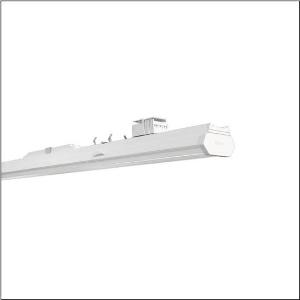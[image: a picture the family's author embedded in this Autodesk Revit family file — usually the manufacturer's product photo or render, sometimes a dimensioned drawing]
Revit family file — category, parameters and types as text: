
# Revit family: licross_11_protected_ho_51tp12dn5exm
name_source: partatom
category: Lighting Fixtures
units: mm (PartAtom-declared; Revit-internal decimal feet)

## family parameters
Cut with Voids When Loaded = No
Host = Face
Light Source = No
Part Type = Normal
Room Calculation Point = No
Round Connector Dimension = Use Diameter
Shared = No

## types (1)
- --- (1 x LED, 14100 lm, 81.2 W, 5000K)
    Apparent Load = 81 VA
    CIE Flux Codes = 70 91 97 98 100
    Color Rendering = 80
    Color Temperature = 5000K
    Default Elevation = 1800 mm
    Description = Licross 11 Protected HO, luminaire insert, of sheet steel, galvanised, coil coated, white, length: 1.500mm, width: 90mm, height: 101mm, LED rated luminous flux: 14.100lm, light colour: 850, SDCM (Standard Deviation of Colour Matching)MacAdam ≤ 2 SDCM (initial), control gear: DALI 2, with plug, 5-pole, with phase selection, mains connection: 220..240V, AC, 50/60Hz, rated input power: 81W, internal wiring halogen-free, primary optical cover: cover, of PMMA, light emission: direct distribution, primary light characteristic: symmetric, protection rating (complete): IP64, insulation class (complete): insulation class I (protective earthing), certification: CE, ENEC, VDE, UKCA, protection symbol: D if used in an environment with conductive dust loads with corresponding accessories, impact resistance: IK06, permissible ambient temperature for indoor applications: -25..+35°C, corresponds to IFS (International Featured Standards) requirements for safety and quality in the food industry, reducing of maximum allowable ambient temperature of 5°C with ceiling mounting, LABS conformity tested according to VDMA 24364:2018-05, The light source and the operating device comply with the requirements of the Ecodesign Regulation (EU) 2019/2020 and are replaceable in accordance with this regulation, packaging unit: 1 piece
    Height = 92 mm
    Lamp = 1 x LED
    Lamp Light Flux = 14100 lm
    Lamp Power = 81.2 W
    Lamp count = 1
    Length = 1500 mm
    Luminous efficacy = 174 lm/W
    Manufacturer = Siteco
    ModVariant = No
    Model = 51TP12DN5EXM
    Mounting Place = Ceiling
    Mounting Type = Pendant
    Number of Poles = 1
    OnlyDefault = Yes
    Power Factor = 1
    Product Name = Licross 11 Protected HO
    Product group = luminaire insert | ceiling pendant
    ProductGroupID = 901
    Protection Class = Protection class I
    Protection Degree = IP 64
    RLX_Detail_Level = 1
    RLX_Emergency_Light_Flux = 0 lm
    RLX_Emergency_Type = 0
    RLX_Emergency_Type_DB = No
    RlxData = <blob elided: 24781 chars, md5=22ba8a19>
    Socket = socket
    Standby Power = 0 W
    System Light Flux = 14100 lm
    System Power = 81 W
    Type Comments = factory setting: luminous flux: 100 % | dim-lin: 254 | 549 mA
    Type Image = l_1256148.jpg
    URL = http://relux.com
    VarID = @adj_021227
    Voltage = 0 V
    Weight = 0.00 kg
    Width = 88 mm

## geometry (parser evidence)
native form markers: Blend x4, Sweep x9
no freeform markers — native parametric forms only
